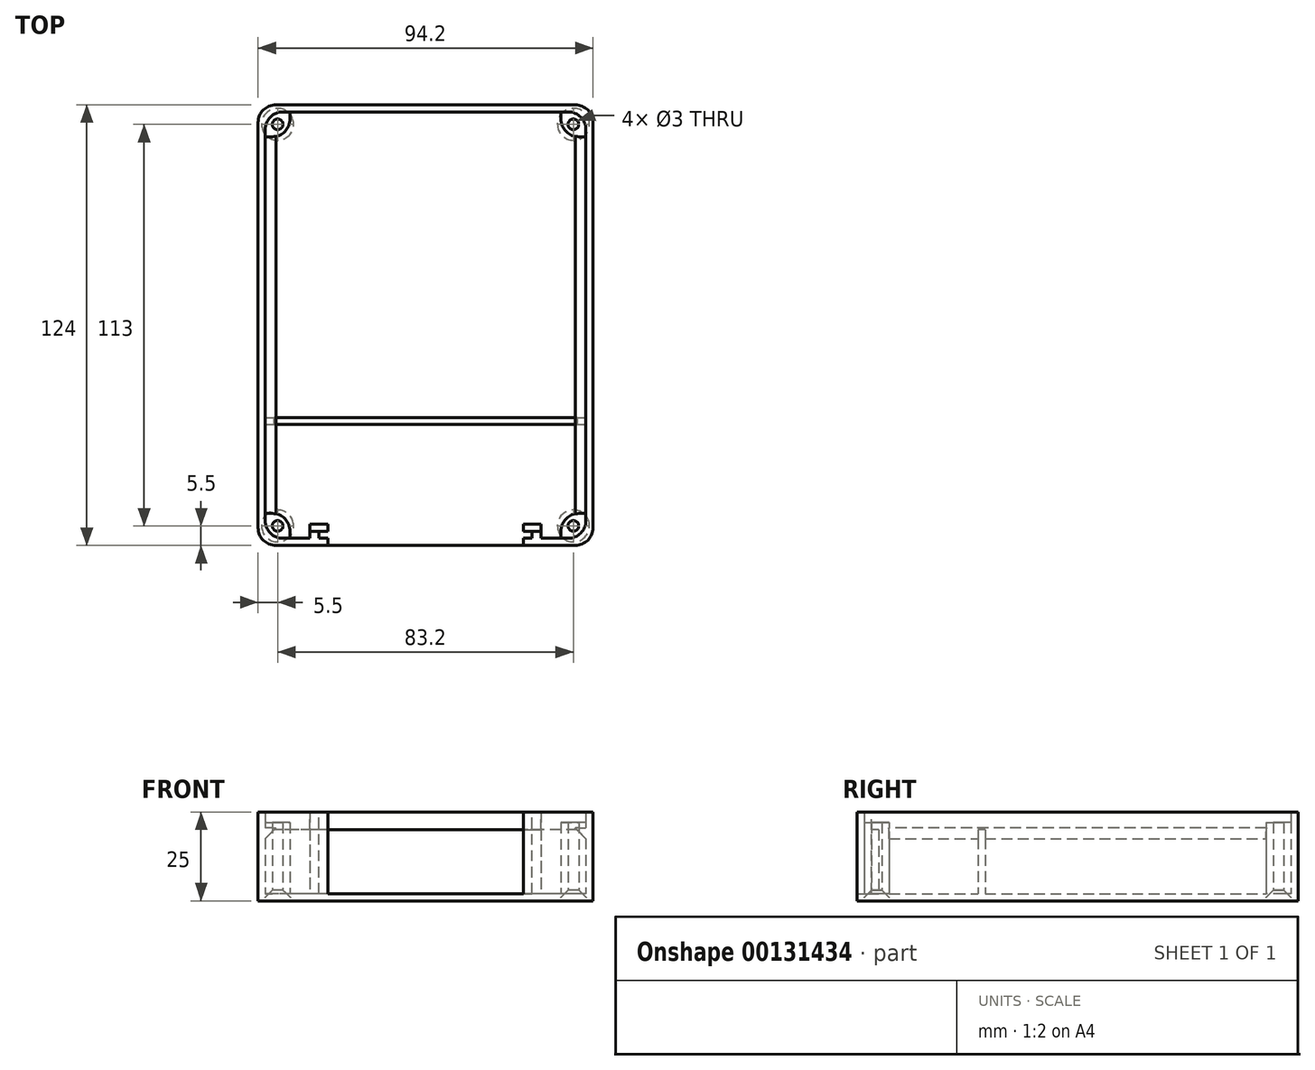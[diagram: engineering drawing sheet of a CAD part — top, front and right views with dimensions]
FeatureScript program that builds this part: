
annotation { "Feature Type Name" : "Feature", "Feature Type Description" : "" }
export const myFeature = defineFeature(function(context is Context, id is Id, definition is map)
    precondition{}
    {
        {
            var Q0;
            Q0=qCreatedBy(makeId("Top.planeOp"),FACE);
            var sketch = newSketch(context, id + "F0", { "sketchPlane" : qUnion([Q0])});
            skLineSegment(sketch, "E0.bottom", {"start": v(45.1, -60) * mm, "end": v(-45.1, -60) * mm});
            skLineSegment(sketch, "E0.top", {"start": v(45.1, 60) * mm, "end": v(-45.1, 60) * mm});
            skLineSegment(sketch, "E0.left", {"start": v(45.1, -60) * mm, "end": v(45.1, 60) * mm});
            skLineSegment(sketch, "E0.right", {"start": v(-45.1, -60) * mm, "end": v(-45.1, 60) * mm});
            skPoint(sketch, "E0.middle", {"position": v(0, 0) * mm});
            skSolve(sketch);
        }
        {
            var Q0;
            Q0=makeQuery(id+"F0.imprint","IMPRINT",FACE,{"disambiguationData":[TD([[makeQuery(id+"F0.imprint","IMPRINT",EDGE,{"derivedFrom":sQuery(id+"F0.wireOp",EDGE,"E0.bottom")}),-1.0]])]});
            extrude(context, id + "F1", {"entities" : qUnion([Q0]), "depth" : 23 * mm});
        }
        {
            var Q0;
            Q0=makeQuery(id+"F1.opExtrude","CAP_FACE",FACE,{"disambiguationData":[OSD([sQuery(id+"F0.wireOp",EDGE,"E0.bottom"),sQuery(id+"F0.wireOp",EDGE,"E0.top"),sQuery(id+"F0.wireOp",EDGE,"E0.left"),sQuery(id+"F0.wireOp",EDGE,"E0.right")])],"isStart":false});
            shell(context, id + "F2", {"entities" : qUnion([Q0]), "thickness" : 2 * mm, "oppositeDirection" : true});
        }
        {
            var Q0;
            Q0=makeQuery(id+"F1.opExtrude","SWEPT_EDGE",EDGE,{"disambiguationData":[OSD([sQuery(id+"F0.wireOp",EDGE,"E0.bottom"),sQuery(id+"F0.wireOp",EDGE,"E0.right")])]});
            var Q1;
            Q1=makeQuery(id+"F1.opExtrude","SWEPT_EDGE",EDGE,{"disambiguationData":[OSD([sQuery(id+"F0.wireOp",EDGE,"E0.bottom"),sQuery(id+"F0.wireOp",EDGE,"E0.left")])]});
            var Q2;
            Q2=makeQuery(id+"F1.opExtrude","SWEPT_EDGE",EDGE,{"disambiguationData":[OSD([sQuery(id+"F0.wireOp",EDGE,"E0.top"),sQuery(id+"F0.wireOp",EDGE,"E0.left")])]});
            var Q3;
            Q3=makeQuery(id+"F1.opExtrude","SWEPT_EDGE",EDGE,{"disambiguationData":[OSD([sQuery(id+"F0.wireOp",EDGE,"E0.top"),sQuery(id+"F0.wireOp",EDGE,"E0.right")])]});
            fillet(context, id + "F3", {"entities" : qUnion([Q0, Q1, Q2, Q3]), "radius" : 5 * mm, "tangentPropagation" : true, "allowEdgeOverflow" : false});
        }
        {
            var Q0;
            Q0=makeQuery(id+"F2.opShell","OFFSET_FACE",FACE,{"disambiguationData":[OSD([sQuery(id+"F0.wireOp",EDGE,"E0.bottom"),sQuery(id+"F0.wireOp",EDGE,"E0.top"),sQuery(id+"F0.wireOp",EDGE,"E0.left"),sQuery(id+"F0.wireOp",EDGE,"E0.right")])]});
            var sketch = newSketch(context, id + "F4", { "sketchPlane" : qUnion([Q0])});
            skLineSegment(sketch, "E1.bottom", {"start": v(-45.1, 60) * mm, "end": v(-38.1, 60) * mm});
            skLineSegment(sketch, "E1.top", {"start": v(-45.1, 53) * mm, "end": v(-38.1, 53) * mm});
            skLineSegment(sketch, "E1.left", {"start": v(-45.1, 60) * mm, "end": v(-45.1, 53) * mm});
            skLineSegment(sketch, "E1.right", {"start": v(-38.1, 60) * mm, "end": v(-38.1, 53) * mm});
            skLineSegment(sketch, "E2.bottom", {"start": v(45.1, 60) * mm, "end": v(38.1, 60) * mm});
            skLineSegment(sketch, "E2.top", {"start": v(45.1, 53) * mm, "end": v(38.1, 53) * mm});
            skLineSegment(sketch, "E2.left", {"start": v(45.1, 60) * mm, "end": v(45.1, 53) * mm});
            skLineSegment(sketch, "E2.right", {"start": v(38.1, 60) * mm, "end": v(38.1, 53) * mm});
            skLineSegment(sketch, "E3.bottom", {"start": v(45.1, -60) * mm, "end": v(38.1, -60) * mm});
            skLineSegment(sketch, "E3.top", {"start": v(45.1, -53) * mm, "end": v(38.1, -53) * mm});
            skLineSegment(sketch, "E3.left", {"start": v(45.1, -60) * mm, "end": v(45.1, -53) * mm});
            skLineSegment(sketch, "E3.right", {"start": v(38.1, -60) * mm, "end": v(38.1, -53) * mm});
            skLineSegment(sketch, "E4.bottom", {"start": v(-45.1, -60) * mm, "end": v(-38.1, -60) * mm});
            skLineSegment(sketch, "E4.top", {"start": v(-45.1, -53) * mm, "end": v(-38.1, -53) * mm});
            skLineSegment(sketch, "E4.left", {"start": v(-45.1, -60) * mm, "end": v(-45.1, -53) * mm});
            skLineSegment(sketch, "E4.right", {"start": v(-38.1, -60) * mm, "end": v(-38.1, -53) * mm});
            skCircle(sketch, "E5", {"center": v(-41.6, 56.5) * mm, "radius": 1.5 * mm});
            skPoint(sketch, "E5.centerSnap0", {"position": v(-38.1, 56.5) * mm});
            skPoint(sketch, "E5.centerSnap1", {"position": v(-41.6, 53) * mm});
            skCircle(sketch, "E6", {"center": v(41.6, 56.5) * mm, "radius": 1.5 * mm});
            skPoint(sketch, "E6.centerSnap0", {"position": v(38.1, 56.5) * mm});
            skPoint(sketch, "E6.centerSnap1", {"position": v(41.6, 53) * mm});
            skCircle(sketch, "E7", {"center": v(-41.6, -56.5) * mm, "radius": 1.5 * mm});
            skPoint(sketch, "E7.centerSnap0", {"position": v(-38.1, -56.5) * mm});
            skPoint(sketch, "E7.centerSnap1", {"position": v(-41.6, -53) * mm});
            skCircle(sketch, "E8", {"center": v(41.6, -56.5) * mm, "radius": 1.5 * mm});
            skPoint(sketch, "E8.centerSnap0", {"position": v(38.1, -56.5) * mm});
            skPoint(sketch, "E8.centerSnap1", {"position": v(41.6, -53) * mm});
            skSolve(sketch);
        }
        {
            var Q0;
            Q0=makeQuery(id+"F4.imprint","IMPRINT",FACE,{"disambiguationData":[TD([[makeQuery(id+"F4.imprint","IMPRINT",EDGE,{"derivedFrom":sQuery(id+"F4.wireOp",EDGE,"E1.bottom")}),1.0]])]});
            var Q1;
            Q1=makeQuery(id+"F4.imprint","IMPRINT",FACE,{"disambiguationData":[TD([[makeQuery(id+"F4.imprint","IMPRINT",EDGE,{"derivedFrom":sQuery(id+"F4.wireOp",EDGE,"E2.bottom")}),1.0]])]});
            var Q2;
            Q2=makeQuery(id+"F4.imprint","IMPRINT",FACE,{"disambiguationData":[TD([[makeQuery(id+"F4.imprint","IMPRINT",EDGE,{"derivedFrom":sQuery(id+"F4.wireOp",EDGE,"E4.bottom")}),-1.0]])]});
            var Q3;
            Q3=makeQuery(id+"F4.imprint","IMPRINT",FACE,{"disambiguationData":[TD([[makeQuery(id+"F4.imprint","IMPRINT",EDGE,{"derivedFrom":sQuery(id+"F4.wireOp",EDGE,"E3.bottom")}),-1.0]])]});
            extrude(context, id + "F5", {"entities" : qUnion([Q0, Q1, Q2, Q3]), "operationType" : NewBodyOperationType.ADD, "depth" : 20 * mm});
        }
        {
            var Q0;
            Q0=makeQuery(id+"F5.opExtrude","SWEPT_FACE",FACE,{"disambiguationData":[OSD([sQuery(id+"F4.wireOp",EDGE,"E3.top")])]});
            var sketch = newSketch(context, id + "F6", { "sketchPlane" : qUnion([Q0])});
            skLineSegment(sketch, "E9", {"start": v(-45.1, 18.5) * mm, "end": v(-45.1, 15.5) * mm});
            skLineSegment(sketch, "E10", {"start": v(-45.1, 15.5) * mm, "end": v(-42.1, 18.5) * mm});
            skLineSegment(sketch, "E11", {"start": v(-42.1, 18.5) * mm, "end": v(-45.1, 18.5) * mm});
            skLineSegment(sketch, "E12", {"start": v(-43.6, 18.5) * mm, "end": v(-43.6, 20) * mm});
            skSolve(sketch);
        }
        {
            var Q0;
            Q0 = qSketchRegion(id + "F6", true);
            var Q1;
            Q1=makeQuery(id+"F6.imprint","IMPRINT",FACE,{"disambiguationData":[TD([[makeQuery(id+"F6.imprint","IMPRINT",EDGE,{"derivedFrom":sQuery(id+"F6.wireOp",EDGE,"E9")}),1.0]])]});
            extrude(context, id + "F7", {"entities" : qUnion([Q0, Q1]), "operationType" : NewBodyOperationType.ADD, "depth" : 106.31 * mm});
        }
        {
            var Q0;
            Q0=makeQuery(id+"F5.opExtrude","SWEPT_FACE",FACE,{"disambiguationData":[OSD([sQuery(id+"F4.wireOp",EDGE,"E1.top")])]});
            var sketch = newSketch(context, id + "F8", { "sketchPlane" : qUnion([Q0])});
            skLineSegment(sketch, "E13", {"start": v(-45.1, 18.5) * mm, "end": v(-45.1, 15.5) * mm});
            skLineSegment(sketch, "E14", {"start": v(-45.1, 15.5) * mm, "end": v(-42.1, 18.5) * mm});
            skLineSegment(sketch, "E15", {"start": v(-42.1, 18.5) * mm, "end": v(-45.1, 18.5) * mm});
            skLineSegment(sketch, "E16", {"start": v(-43.6, 18.5) * mm, "end": v(-43.6, 20) * mm});
            skPoint(sketch, "E16.endSnap0", {"position": v(-41.6, 20) * mm});
            skSolve(sketch);
        }
        {
            var Q0;
            {var subQ0=sQuery(id+"F8.wireOp",EDGE,"E13");Q0=makeQuery(id+"F8.imprint","IMPRINT",FACE,{"disambiguationData":[TD([[makeQuery(id+"F8.imprint","IMPRINT",EDGE,{"derivedFrom":subQ0}),1.0]])]});}
            extrude(context, id + "F9", {"entities" : qUnion([Q0]), "operationType" : NewBodyOperationType.ADD, "depth" : 106.4 * mm});
        }
        {
            var Q0;
            Q0=makeQuery(id+"F5.opExtrude","SWEPT_EDGE",EDGE,{"disambiguationData":[OSD([sQuery(id+"F4.wireOp",EDGE,"E4.top"),sQuery(id+"F4.wireOp",EDGE,"E4.right")])]});
            var Q1;
            Q1=makeQuery(id+"F5.opExtrude","SWEPT_EDGE",EDGE,{"disambiguationData":[OSD([sQuery(id+"F4.wireOp",EDGE,"E1.top"),sQuery(id+"F4.wireOp",EDGE,"E1.right")])]});
            var Q2;
            Q2=makeQuery(id+"F5.opExtrude","SWEPT_EDGE",EDGE,{"disambiguationData":[OSD([sQuery(id+"F4.wireOp",EDGE,"E3.top"),sQuery(id+"F4.wireOp",EDGE,"E3.right")])]});
            var Q3;
            Q3=makeQuery(id+"F5.opExtrude","SWEPT_EDGE",EDGE,{"disambiguationData":[OSD([sQuery(id+"F4.wireOp",EDGE,"E2.top"),sQuery(id+"F4.wireOp",EDGE,"E2.right")])]});
            fillet(context, id + "F10", {"entities" : qUnion([Q0, Q1, Q2, Q3]), "radius" : 5 * mm, "tangentPropagation" : true, "allowEdgeOverflow" : false});
        }
        {
            var Q0;
            Q0=makeQuery(id+"F5.boolean.opBoolean","SPLIT",FACE,{"disambiguationData":[TD([makeQuery(id+"F5.opExtrude","SWEPT_FACE",FACE,{"disambiguationData":[OSD([sQuery(id+"F4.wireOp",EDGE,"E5")])]})])],"derivedFrom":makeQuery(id+"F2.opShell","OFFSET_FACE",FACE,{"disambiguationData":[OSD([sQuery(id+"F0.wireOp",EDGE,"E0.bottom"),sQuery(id+"F0.wireOp",EDGE,"E0.top"),sQuery(id+"F0.wireOp",EDGE,"E0.left"),sQuery(id+"F0.wireOp",EDGE,"E0.right")])]})});
            extrude(context, id + "F11", {"entities" : qUnion([Q0]), "operationType" : NewBodyOperationType.REMOVE, "endBound" : BoundingType.THROUGH_ALL, "oppositeDirection" : true, "depth" : 25 * mm});
        }
        {
            var Q0;
            Q0=makeQuery(id+"F5.boolean.opBoolean","SPLIT",FACE,{"disambiguationData":[TD([makeQuery(id+"F5.opExtrude","SWEPT_FACE",FACE,{"disambiguationData":[OSD([sQuery(id+"F4.wireOp",EDGE,"E6")])]})])],"derivedFrom":makeQuery(id+"F2.opShell","OFFSET_FACE",FACE,{"disambiguationData":[OSD([sQuery(id+"F0.wireOp",EDGE,"E0.bottom"),sQuery(id+"F0.wireOp",EDGE,"E0.top"),sQuery(id+"F0.wireOp",EDGE,"E0.left"),sQuery(id+"F0.wireOp",EDGE,"E0.right")])]})});
            extrude(context, id + "F12", {"entities" : qUnion([Q0]), "operationType" : NewBodyOperationType.REMOVE, "endBound" : BoundingType.THROUGH_ALL, "oppositeDirection" : true, "depth" : 25 * mm});
        }
        {
            var Q0;
            Q0=makeQuery(id+"F5.boolean.opBoolean","SPLIT",FACE,{"disambiguationData":[TD([makeQuery(id+"F5.opExtrude","SWEPT_FACE",FACE,{"disambiguationData":[OSD([sQuery(id+"F4.wireOp",EDGE,"E7")])]})])],"derivedFrom":makeQuery(id+"F2.opShell","OFFSET_FACE",FACE,{"disambiguationData":[OSD([sQuery(id+"F0.wireOp",EDGE,"E0.bottom"),sQuery(id+"F0.wireOp",EDGE,"E0.top"),sQuery(id+"F0.wireOp",EDGE,"E0.left"),sQuery(id+"F0.wireOp",EDGE,"E0.right")])]})});
            extrude(context, id + "F13", {"entities" : qUnion([Q0]), "operationType" : NewBodyOperationType.REMOVE, "endBound" : BoundingType.THROUGH_ALL, "oppositeDirection" : true, "depth" : 25 * mm});
        }
        {
            var Q0;
            Q0=makeQuery(id+"F5.boolean.opBoolean","SPLIT",FACE,{"disambiguationData":[TD([makeQuery(id+"F5.opExtrude","SWEPT_FACE",FACE,{"disambiguationData":[OSD([sQuery(id+"F4.wireOp",EDGE,"E8")])]})])],"derivedFrom":makeQuery(id+"F2.opShell","OFFSET_FACE",FACE,{"disambiguationData":[OSD([sQuery(id+"F0.wireOp",EDGE,"E0.bottom"),sQuery(id+"F0.wireOp",EDGE,"E0.top"),sQuery(id+"F0.wireOp",EDGE,"E0.left"),sQuery(id+"F0.wireOp",EDGE,"E0.right")])]})});
            extrude(context, id + "F14", {"entities" : qUnion([Q0]), "operationType" : NewBodyOperationType.REMOVE, "endBound" : BoundingType.THROUGH_ALL, "oppositeDirection" : true, "depth" : 25 * mm});
        }
        {
            var Q0;
            Q0=makeQuery(id+"F13.boolean.opBoolean","INTERSECT",EDGE,{"derivedFrom":[makeQuery(id+"F1.opExtrude","CAP_FACE",FACE,{"disambiguationData":[OSD([sQuery(id+"F0.wireOp",EDGE,"E0.bottom"),sQuery(id+"F0.wireOp",EDGE,"E0.top"),sQuery(id+"F0.wireOp",EDGE,"E0.left"),sQuery(id+"F0.wireOp",EDGE,"E0.right")])],"isStart":true}),makeQuery(id+"F13.opExtrude","SWEPT_FACE",FACE,{"disambiguationData":[OSD([sQuery(id+"F4.wireOp",EDGE,"E7")])]})]});
            var Q1;
            Q1=makeQuery(id+"F14.boolean.opBoolean","INTERSECT",EDGE,{"derivedFrom":[makeQuery(id+"F1.opExtrude","CAP_FACE",FACE,{"disambiguationData":[OSD([sQuery(id+"F0.wireOp",EDGE,"E0.bottom"),sQuery(id+"F0.wireOp",EDGE,"E0.top"),sQuery(id+"F0.wireOp",EDGE,"E0.left"),sQuery(id+"F0.wireOp",EDGE,"E0.right")])],"isStart":true}),makeQuery(id+"F14.opExtrude","SWEPT_FACE",FACE,{"disambiguationData":[OSD([sQuery(id+"F4.wireOp",EDGE,"E8")])]})]});
            var Q2;
            Q2=makeQuery(id+"F12.boolean.opBoolean","INTERSECT",EDGE,{"derivedFrom":[makeQuery(id+"F1.opExtrude","CAP_FACE",FACE,{"disambiguationData":[OSD([sQuery(id+"F0.wireOp",EDGE,"E0.bottom"),sQuery(id+"F0.wireOp",EDGE,"E0.top"),sQuery(id+"F0.wireOp",EDGE,"E0.left"),sQuery(id+"F0.wireOp",EDGE,"E0.right")])],"isStart":true}),makeQuery(id+"F12.opExtrude","SWEPT_FACE",FACE,{"disambiguationData":[OSD([sQuery(id+"F4.wireOp",EDGE,"E6")])]})]});
            var Q3;
            Q3=makeQuery(id+"F11.boolean.opBoolean","INTERSECT",EDGE,{"derivedFrom":[makeQuery(id+"F1.opExtrude","CAP_FACE",FACE,{"disambiguationData":[OSD([sQuery(id+"F0.wireOp",EDGE,"E0.bottom"),sQuery(id+"F0.wireOp",EDGE,"E0.top"),sQuery(id+"F0.wireOp",EDGE,"E0.left"),sQuery(id+"F0.wireOp",EDGE,"E0.right")])],"isStart":true}),makeQuery(id+"F11.opExtrude","SWEPT_FACE",FACE,{"disambiguationData":[OSD([sQuery(id+"F4.wireOp",EDGE,"E5")])]})]});
            chamfer(context, id + "F15", {"entities" : qUnion([Q0, Q1, Q2, Q3]), "width" : 3 * mm, "tangentPropagation" : true});
        }
        {
            var Q0;
            Q0=makeQuery(id+"F2.opShell","OFFSET_EDGE",EDGE,{"disambiguationData":[OSD([sQuery(id+"F0.wireOp",EDGE,"E0.bottom"),sQuery(id+"F0.wireOp",EDGE,"E0.right")])]});
            var Q1;
            Q1=makeQuery(id+"F2.opShell","OFFSET_EDGE",EDGE,{"disambiguationData":[OSD([sQuery(id+"F0.wireOp",EDGE,"E0.top"),sQuery(id+"F0.wireOp",EDGE,"E0.right")])]});
            var Q2;
            Q2=makeQuery(id+"F2.opShell","OFFSET_EDGE",EDGE,{"disambiguationData":[OSD([sQuery(id+"F0.wireOp",EDGE,"E0.bottom"),sQuery(id+"F0.wireOp",EDGE,"E0.left")])]});
            var Q3;
            Q3=makeQuery(id+"F2.opShell","OFFSET_EDGE",EDGE,{"disambiguationData":[OSD([sQuery(id+"F0.wireOp",EDGE,"E0.top"),sQuery(id+"F0.wireOp",EDGE,"E0.left")])]});
            fillet(context, id + "F16", {"entities" : qUnion([Q0, Q1, Q2, Q3]), "radius" : 5 * mm, "tangentPropagation" : true, "allowEdgeOverflow" : false});
        }
        {
            var Q0;
            {var subQ0=sQuery(id+"F0.wireOp",EDGE,"E0.top");var subQ1=sQuery(id+"F0.wireOp",EDGE,"E0.bottom");var subQ2=sQuery(id+"F0.wireOp",EDGE,"E0.right");var subQ3=sQuery(id+"F0.wireOp",EDGE,"E0.left");Q0=makeQuery(id+"FUXcTS6dqTLmqvX_1.boolean.opBoolean","MERGE",FACE,{"derivedFrom":[makeQuery(id+"F5.boolean.opBoolean","SPLIT",FACE,{"disambiguationData":[TD([makeQuery(id+"F2.opShell","OFFSET_FACE",FACE,{"disambiguationData":[OSD([subQ1])]})])],"derivedFrom":makeQuery(id+"F2.opShell","OFFSET_FACE",FACE,{"disambiguationData":[OSD([subQ1,subQ0,subQ3,subQ2])]})}),makeQuery(id+"FUXcTS6dqTLmqvX_1.opExtrude","CAP_FACE",FACE,{"disambiguationData":[OSD([sQuery(id+"FIoK9KxFrZt5bui_1.wireOp",EDGE,"LDbmhA7z-1XxK-v0uN-PiKb-zhcR89wiue6D.bottom"),sQuery(id+"FIoK9KxFrZt5bui_1.wireOp",EDGE,"LDbmhA7z-1XxK-v0uN-PiKb-zhcR89wiue6D.top"),sQuery(id+"FIoK9KxFrZt5bui_1.wireOp",EDGE,"LDbmhA7z-1XxK-v0uN-PiKb-zhcR89wiue6D.left"),sQuery(id+"FIoK9KxFrZt5bui_1.wireOp",EDGE,"LDbmhA7z-1XxK-v0uN-PiKb-zhcR89wiue6D.right"),sQuery(id+"FIoK9KxFrZt5bui_1.wireOp",EDGE,"4bVF4LJQ-03n9-MwA0-47bT-3AlnKOSisqOL.top"),sQuery(id+"FIoK9KxFrZt5bui_1.wireOp",EDGE,"4bVF4LJQ-03n9-MwA0-47bT-3AlnKOSisqOL.left"),sQuery(id+"FIoK9KxFrZt5bui_1.wireOp",EDGE,"4bVF4LJQ-03n9-MwA0-47bT-3AlnKOSisqOL.right"),sQuery(id+"FIoK9KxFrZt5bui_1.wireOp",EDGE,"Ixqmyhyf-sNDO-FMaM-q0U5-mh7TiLs3qJI1.top"),sQuery(id+"FIoK9KxFrZt5bui_1.wireOp",EDGE,"Ixqmyhyf-sNDO-FMaM-q0U5-mh7TiLs3qJI1.left"),sQuery(id+"FIoK9KxFrZt5bui_1.wireOp",EDGE,"Ixqmyhyf-sNDO-FMaM-q0U5-mh7TiLs3qJI1.right")])],"isStart":false})]});}
            var sketch = newSketch(context, id + "F17", { "sketchPlane" : qUnion([Q0])});
            skLineSegment(sketch, "E17.bottom", {"start": v(45.1, -28) * mm, "end": v(-45.1, -28) * mm});
            skLineSegment(sketch, "E17.top", {"start": v(45.1, -26) * mm, "end": v(-45.1, -26) * mm});
            skLineSegment(sketch, "E17.left", {"start": v(45.1, -28) * mm, "end": v(45.1, -26) * mm});
            skLineSegment(sketch, "E17.right", {"start": v(-45.1, -28) * mm, "end": v(-45.1, -26) * mm});
            skLineSegment(sketch, "E18", {"start": v(0, -28) * mm, "end": v(0, -60) * mm});
            skSolve(sketch);
        }
        {
            var Q0;
            Q0 = qSketchRegion(id + "F17", true);
            var Q1;
            Q1=makeQuery(id+"F17.imprint","IMPRINT",FACE,{"disambiguationData":[TD([[makeQuery(id+"F17.imprint","IMPRINT",EDGE,{"derivedFrom":sQuery(id+"F17.wireOp",EDGE,"E17.bottom")}),-1.0]])]});
            extrude(context, id + "F18", {"entities" : qUnion([Q0, Q1]), "operationType" : NewBodyOperationType.ADD, "depth" : 18 * mm});
        }
        {
            var Q0;
            Q0=makeQuery(id+"F2.opShell","OFFSET_FACE",FACE,{"disambiguationData":[OSD([sQuery(id+"F0.wireOp",EDGE,"E0.bottom")])]});
            var sketch = newSketch(context, id + "F19", { "sketchPlane" : qUnion([Q0])});
            skLineSegment(sketch, "E19.bottom", {"start": v(-32.5, 23) * mm, "end": v(32.5, 23) * mm});
            skLineSegment(sketch, "E19.top", {"start": v(-32.5, 0) * mm, "end": v(32.5, 0) * mm});
            skLineSegment(sketch, "E19.left", {"start": v(-32.5, 23) * mm, "end": v(-32.5, 0) * mm});
            skLineSegment(sketch, "E19.right", {"start": v(32.5, 23) * mm, "end": v(32.5, 0) * mm});
            skLineSegment(sketch, "E20", {"start": v(0, 0) * mm, "end": v(0, 0) * mm});
            skSolve(sketch);
        }
        {
            var Q0;
            Q0 = qSketchRegion(id + "F19", true);
            extrude(context, id + "F20", {"entities" : qUnion([Q0]), "operationType" : NewBodyOperationType.ADD, "depth" : 4 * mm});
        }
        {
            var Q0;
            Q0=makeQuery(id+"F20.boolean.opBoolean","MERGE",FACE,{"derivedFrom":[makeQuery(id+"F1.opExtrude","CAP_FACE",FACE,{"disambiguationData":[OSD([sQuery(id+"F0.wireOp",EDGE,"E0.bottom"),sQuery(id+"F0.wireOp",EDGE,"E0.top"),sQuery(id+"F0.wireOp",EDGE,"E0.left"),sQuery(id+"F0.wireOp",EDGE,"E0.right")])],"isStart":false}),makeQuery(id+"F20.opExtrude","SWEPT_FACE",FACE,{"disambiguationData":[OSD([sQuery(id+"F19.wireOp",EDGE,"E19.bottom")])]})]});
            var sketch = newSketch(context, id + "F21", { "sketchPlane" : qUnion([Q0])});
            skLineSegment(sketch, "E21.bottom", {"start": v(-27.5, -62) * mm, "end": v(27.5, -62) * mm});
            skLineSegment(sketch, "E21.top", {"start": v(-27.5, -56) * mm, "end": v(27.5, -56) * mm});
            skLineSegment(sketch, "E21.left", {"start": v(-27.5, -62) * mm, "end": v(-27.5, -56) * mm});
            skLineSegment(sketch, "E21.right", {"start": v(27.5, -62) * mm, "end": v(27.5, -56) * mm});
            skLineSegment(sketch, "E22", {"start": v(0, -56) * mm, "end": v(0, -56) * mm});
            skLineSegment(sketch, "E23.bottom", {"start": v(27.5, -58) * mm, "end": v(30, -58) * mm});
            skLineSegment(sketch, "E23.top", {"start": v(27.5, -60) * mm, "end": v(30, -60) * mm});
            skLineSegment(sketch, "E23.left", {"start": v(27.5, -58) * mm, "end": v(27.5, -60) * mm});
            skLineSegment(sketch, "E23.right", {"start": v(30, -58) * mm, "end": v(30, -60) * mm});
            skLineSegment(sketch, "E24.bottom", {"start": v(-27.5, -60) * mm, "end": v(-30, -60) * mm});
            skLineSegment(sketch, "E24.top", {"start": v(-27.5, -58) * mm, "end": v(-30, -58) * mm});
            skLineSegment(sketch, "E24.left", {"start": v(-27.5, -60) * mm, "end": v(-27.5, -58) * mm});
            skLineSegment(sketch, "E24.right", {"start": v(-30, -60) * mm, "end": v(-30, -58) * mm});
            skLineSegment(sketch, "E25", {"start": v(-28.75, -58) * mm, "end": v(-28.75, -56) * mm});
            skLineSegment(sketch, "E26", {"start": v(28.75, -58) * mm, "end": v(28.75, -56) * mm});
            skSolve(sketch);
        }
        {
            var Q0;
            {var subQ5=sQuery(id+"F21.wireOp",EDGE,"E21.bottom");Q0=makeQuery(id+"F21.imprint","IMPRINT",FACE,{"disambiguationData":[TD([[makeQuery(id+"F21.imprint","IMPRINT",EDGE,{"derivedFrom":subQ5}),-1.0]])]});}
            var Q1;
            Q1=makeQuery(id+"F21.imprint","IMPRINT",FACE,{"disambiguationData":[TD([[makeQuery(id+"F21.imprint","IMPRINT",EDGE,{"derivedFrom":sQuery(id+"F21.wireOp",EDGE,"E24.bottom")}),-1.0]])]});
            var Q2;
            Q2=makeQuery(id+"F21.imprint","IMPRINT",FACE,{"disambiguationData":[TD([[makeQuery(id+"F21.imprint","IMPRINT",EDGE,{"derivedFrom":sQuery(id+"F21.wireOp",EDGE,"E23.top")}),1.0]])]});
            extrude(context, id + "F22", {"entities" : qUnion([Q0, Q1, Q2]), "operationType" : NewBodyOperationType.REMOVE, "oppositeDirection" : true, "depth" : 23 * mm});
        }
        {
            var Q0;
            Q0=makeQuery(id+"F20.boolean.opBoolean","MERGE",FACE,{"derivedFrom":[makeQuery(id+"F1.opExtrude","CAP_FACE",FACE,{"disambiguationData":[OSD([sQuery(id+"F0.wireOp",EDGE,"E0.bottom"),sQuery(id+"F0.wireOp",EDGE,"E0.top"),sQuery(id+"F0.wireOp",EDGE,"E0.left"),sQuery(id+"F0.wireOp",EDGE,"E0.right")])],"isStart":false}),makeQuery(id+"F20.opExtrude","SWEPT_FACE",FACE,{"disambiguationData":[OSD([sQuery(id+"F19.wireOp",EDGE,"E19.bottom")])]})]});
            var sketch = newSketch(context, id + "F23", { "sketchPlane" : qUnion([Q0])});
            skLineSegment(sketch, "E27.bottom", {"start": v(-27.5, -58) * mm, "end": v(-32.5, -58) * mm});
            skLineSegment(sketch, "E27.top", {"start": v(-27.5, -56) * mm, "end": v(-32.5, -56) * mm});
            skLineSegment(sketch, "E27.left", {"start": v(-27.5, -58) * mm, "end": v(-27.5, -56) * mm});
            skLineSegment(sketch, "E27.right", {"start": v(-32.5, -58) * mm, "end": v(-32.5, -56) * mm});
            skLineSegment(sketch, "E28.bottom", {"start": v(27.5, -58) * mm, "end": v(32.5, -58) * mm});
            skLineSegment(sketch, "E28.top", {"start": v(27.5, -56) * mm, "end": v(32.5, -56) * mm});
            skLineSegment(sketch, "E28.left", {"start": v(27.5, -58) * mm, "end": v(27.5, -56) * mm});
            skLineSegment(sketch, "E28.right", {"start": v(32.5, -58) * mm, "end": v(32.5, -56) * mm});
            skSolve(sketch);
        }
        {
            var Q0;
            Q0 = qSketchRegion(id + "F23", true);
            var Q1;
            Q1=makeQuery(id+"F23.imprint","IMPRINT",FACE,{"disambiguationData":[TD([[makeQuery(id+"F23.imprint","IMPRINT",EDGE,{"derivedFrom":sQuery(id+"F23.wireOp",EDGE,"E27.top")}),1.0]])]});
            extrude(context, id + "F24", {"entities" : qUnion([Q0, Q1]), "operationType" : NewBodyOperationType.REMOVE, "oppositeDirection" : true, "depth" : 5 * mm});
        }
    });
